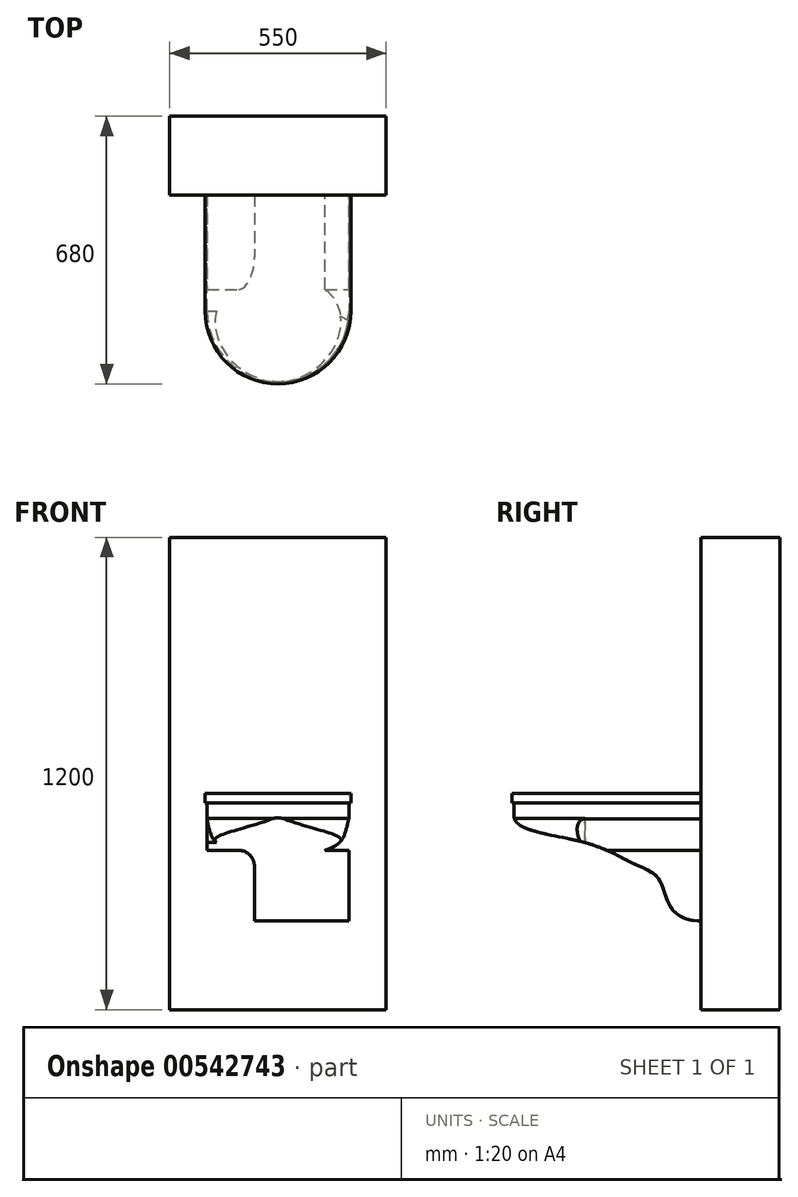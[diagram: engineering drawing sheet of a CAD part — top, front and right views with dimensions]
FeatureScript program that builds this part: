
annotation { "Feature Type Name" : "Feature", "Feature Type Description" : "" }
export const myFeature = defineFeature(function(context is Context, id is Id, definition is map)
    precondition{}
    {
        {
            var Q0;
            Q0=qCreatedBy(makeId("Top.planeOp"),FACE);
            var sketch = newSketch(context, id + "F0", { "sketchPlane" : qUnion([Q0])});
            skArc(sketch, "E0", {"start": v(-185, -300) * mm, "mid": v(0, -485) * mm, "end": v(185, -300) * mm});
            skLineSegment(sketch, "E1.bottom", {"start": v(185, 0) * mm, "end": v(-185, 0) * mm});
            skLineSegment(sketch, "E1.left", {"start": v(185, 0) * mm, "end": v(185, -300) * mm});
            skLineSegment(sketch, "E1.right", {"start": v(-185, 0) * mm, "end": v(-185, -300) * mm});
            skPoint(sketch, "E1.middle", {"position": v(0, -150) * mm});
            skSolve(sketch);
        }
        {
            var Q0;
            Q0 = qSketchRegion(id + "F0", true);
            extrude(context, id + "F1", {"entities" : qUnion([Q0]), "depth" : 25 * mm, "offsetDistance" : 25 * mm});
        }
        {
            var Q0;
            Q0=makeQuery(id+"F1.opExtrude","CAP_FACE",FACE,{"disambiguationData":[OSD([sQuery(id+"F0.wireOp",EDGE,"E0"),sQuery(id+"F0.wireOp",EDGE,"E1.bottom"),sQuery(id+"F0.wireOp",EDGE,"E1.left"),sQuery(id+"F0.wireOp",EDGE,"E1.right")])],"isStart":true});
            var sketch = newSketch(context, id + "F2", { "sketchPlane" : qUnion([Q0])});
            skLineSegment(sketch, "E2.0", {"start": v(180, 5) * mm, "end": v(180, 300) * mm});
            skLineSegment(sketch, "E2.1", {"start": v(-180, 5) * mm, "end": v(180, 5) * mm});
            skLineSegment(sketch, "E2.2", {"start": v(-180, 300) * mm, "end": v(-180, 5) * mm});
            skArc(sketch, "E2.3", {"start": v(180, 300) * mm, "mid": v(0, 480) * mm, "end": v(-180, 300) * mm});
            skSolve(sketch);
        }
        {
            var Q0;
            Q0 = qSketchRegion(id + "F2", true);
            extrude(context, id + "F3", {"entities" : qUnion([Q0]), "operationType" : NewBodyOperationType.ADD, "depth" : 300 * mm, "offsetDistance" : 25 * mm});
        }
        {
            var Q0;
            Q0=qCreatedBy(makeId("Right.planeOp"),FACE);
            var sketch = newSketch(context, id + "F4", { "sketchPlane" : qUnion([Q0])});
            skFitSpline(sketch, "E3", {"points": [v(-480, -37.2) * mm, v(-304.94, -99.2) * mm, v(-175.97, -154.01) * mm, v(-118.02, -186.5) * mm, v(-93.23, -241.22) * mm, v(-5, -300) * mm], "startDerivative": vector(65.09, -404.92) * mm, "endDerivative": vector(902.43, 0) * mm});
            skLineSegment(sketch, "E4", {"start": v(-480, -37.2) * mm, "end": v(-480, -300) * mm});
            skLineSegment(sketch, "E5", {"start": v(-480, -300) * mm, "end": v(-5, -300) * mm});
            skSolve(sketch);
        }
        {
            var Q0;
            Q0 = qSketchRegion(id + "F4", true);
            extrude(context, id + "F5", {"entities" : qUnion([Q0]), "operationType" : NewBodyOperationType.REMOVE, "oppositeDirection" : true, "depth" : 370 * mm, "offsetDistance" : 25 * mm, "symmetric" : true});
        }
        {
            var Q0;
            Q0=makeQuery(id+"F1.opExtrude","CAP_FACE",FACE,{"disambiguationData":[OSD([sQuery(id+"F0.wireOp",EDGE,"E0"),sQuery(id+"F0.wireOp",EDGE,"E1.bottom"),sQuery(id+"F0.wireOp",EDGE,"E1.left"),sQuery(id+"F0.wireOp",EDGE,"E1.right")])],"isStart":true});
            cPlane(context, id + "F6", {"entities" : qUnion([Q0]), "cplaneType" : CPlaneType.OFFSET, "offset" : 120 * mm, "width" : 150 * mm, "height" : 150 * mm});
        }
        {
            var Q0;
            Q0=qCreatedBy(id+"F6.planeOp",FACE);
            var sketch = newSketch(context, id + "F7", { "sketchPlane" : qUnion([Q0])});
            skLineSegment(sketch, "E6.bottom", {"start": v(-185, 0) * mm, "end": v(-60, 0) * mm});
            skLineSegment(sketch, "E6.top", {"start": v(-185, 370) * mm, "end": v(-60, 370) * mm});
            skLineSegment(sketch, "E6.left", {"start": v(-185, 0) * mm, "end": v(-185, 370) * mm});
            skLineSegment(sketch, "E6.right", {"start": v(-60, 0) * mm, "end": v(-60, 370) * mm});
            skSolve(sketch);
        }
        {
            var Q0;
            Q0 = qSketchRegion(id + "F7", true);
            extrude(context, id + "F8", {"entities" : qUnion([Q0]), "operationType" : NewBodyOperationType.REMOVE, "endBound" : BoundingType.UP_TO_NEXT, "depth" : 25 * mm, "offsetDistance" : 25 * mm});
        }
        {
            var Q0;
            Q0=makeQuery(id+"FyPkYtJmn28z9xq_1.1.F8.boolean.opBoolean","COPY",EDGE,{"derivedFrom":makeQuery(id+"FyPkYtJmn28z9xq_1.1.F8.opExtrude","CAP_EDGE",EDGE,{"disambiguationData":[OSD([sQuery(id+"F7.wireOp",EDGE,"E6.right")])],"isStart":true})});
            var Q1;
            Q1=makeQuery(id+"F8.boolean.opBoolean","COPY",EDGE,{"derivedFrom":makeQuery(id+"F8.opExtrude","CAP_EDGE",EDGE,{"disambiguationData":[OSD([sQuery(id+"F7.wireOp",EDGE,"E6.right")])],"isStart":true})});
            var Q2;
            Q2=makeQuery(id+"F8.boolean.opBoolean","COPY",EDGE,{"derivedFrom":makeQuery(id+"F8.opExtrude","TWEAK_EDGE",EDGE,{"derivedFrom":[makeQuery(id+"F5.boolean.opBoolean","COPY",FACE,{"derivedFrom":makeQuery(id+"F5.opExtrude","SWEPT_FACE",FACE,{"disambiguationData":[OSD([sQuery(id+"F4.wireOp",EDGE,"E3")])]})}),makeQuery(id+"F7.imprint","IMPRINT",EDGE,{"derivedFrom":sQuery(id+"F7.wireOp",EDGE,"E6.right")})]})});
            var Q3;
            Q3=makeQuery(id+"FyPkYtJmn28z9xq_1.1.F8.boolean.opBoolean","COPY",EDGE,{"derivedFrom":makeQuery(id+"FyPkYtJmn28z9xq_1.1.F8.opExtrude","TWEAK_EDGE",EDGE,{"derivedFrom":[makeQuery(id+"F7.imprint","IMPRINT",EDGE,{"derivedFrom":sQuery(id+"F7.wireOp",EDGE,"E6.right")}),makeQuery(id+"F5.boolean.opBoolean","COPY",FACE,{"derivedFrom":makeQuery(id+"F5.opExtrude","SWEPT_FACE",FACE,{"disambiguationData":[OSD([sQuery(id+"F4.wireOp",EDGE,"E3")])]})})]})});
            fillet(context, id + "F9", {"entities" : qUnion([Q0, Q1, Q2, Q3]), "radius" : 40 * mm, "tangentPropagation" : true, "allowEdgeOverflow" : false});
        }
        {
            var Q0;
            Q0=qCreatedBy(makeId("Front.planeOp"),FACE);
            var sketch = newSketch(context, id + "F10", { "sketchPlane" : qUnion([Q0])});
            skLineSegment(sketch, "E7", {"start": v(180, -120) * mm, "end": v(180, -40) * mm});
            skLineSegment(sketch, "E8", {"start": v(180, -120) * mm, "end": v(120, -120) * mm});
            skFitSpline(sketch, "E9", {"points": [v(180, -40) * mm, v(160.88, -95.13) * mm, v(120, -120) * mm], "startDerivative": vector(-25.95, -96.42) * mm, "endDerivative": vector(-99.17, -37.79) * mm});
            skSolve(sketch);
        }
        {
            var Q0;
            Q0 = qSketchRegion(id + "F10", true);
            extrude(context, id + "F11", {"entities" : qUnion([Q0]), "operationType" : NewBodyOperationType.REMOVE, "endBound" : BoundingType.THROUGH_ALL, "depth" : 25 * mm, "offsetDistance" : 25 * mm});
        }
        {
            var Q0;
            Q0=qCreatedBy(makeId("Front.planeOp"),FACE);
            cPlane(context, id + "F12", {"entities" : qUnion([Q0]), "cplaneType" : CPlaneType.OFFSET, "offset" : 300 * mm, "width" : 150 * mm, "height" : 150 * mm});
        }
        {
            var Q0;
            Q0=qCreatedBy(id+"F12.planeOp",FACE);
            var sketch = newSketch(context, id + "F13", { "sketchPlane" : qUnion([Q0])});
            skFitSpline(sketch, "E10", {"points": [v(-180, -39.7) * mm, v(-158.09, -99.12) * mm, v(-113.4, -120) * mm], "startDerivative": vector(20.74, -134.03) * mm, "endDerivative": vector(107.54, -26.6) * mm});
            skLineSegment(sketch, "E11", {"start": v(0, 0) * mm, "end": v(0, -129.51) * mm});
            skLineSegment(sketch, "E12", {"start": v(-180, -39.7) * mm, "end": v(-215.7, -39.7) * mm});
            skLineSegment(sketch, "E13", {"start": v(-215.7, -39.7) * mm, "end": v(-215.7, -142.67) * mm});
            skLineSegment(sketch, "E14", {"start": v(-113.4, -120) * mm, "end": v(-66.91, -142.67) * mm});
            skLineSegment(sketch, "E15", {"start": v(-66.91, -142.67) * mm, "end": v(-215.7, -142.67) * mm});
            skSolve(sketch);
        }
        {
            var Q0;
            Q0 = qSketchRegion(id + "F13", true);
            var Q1;
            Q1=sQuery(id+"F13.wireOp",EDGE,"E11");
            revolve(context, id + "F14", {"operationType" : NewBodyOperationType.REMOVE, "entities" : qUnion([Q0]), "axis" : qUnion([Q1]), "revolveType" : RevolveType.ONE_DIRECTION, "oppositeDirection" : true, "angle" : 180 * degree});
        }
        {
            var Q0;
            Q0=makeQuery(id+"F3.opExtrude","SWEPT_FACE",FACE,{"disambiguationData":[OSD([sQuery(id+"F2.wireOp",EDGE,"E2.1")])]});
            var sketch = newSketch(context, id + "F15", { "sketchPlane" : qUnion([Q0])});
            skLineSegment(sketch, "E16.bottom", {"start": v(275, 675) * mm, "end": v(-275, 675) * mm});
            skLineSegment(sketch, "E16.top", {"start": v(275, -525) * mm, "end": v(-275, -525) * mm});
            skLineSegment(sketch, "E16.left", {"start": v(275, 675) * mm, "end": v(275, -525) * mm});
            skLineSegment(sketch, "E16.right", {"start": v(-275, 675) * mm, "end": v(-275, -525) * mm});
            skPoint(sketch, "E16.middle", {"position": v(0, 75) * mm});
            skSolve(sketch);
        }
        {
            var Q0;
            Q0 = qSketchRegion(id + "F15", true);
            extrude(context, id + "F16", {"entities" : qUnion([Q0]), "operationType" : NewBodyOperationType.ADD, "depth" : 200 * mm, "offsetDistance" : 25 * mm});
        }
    });
